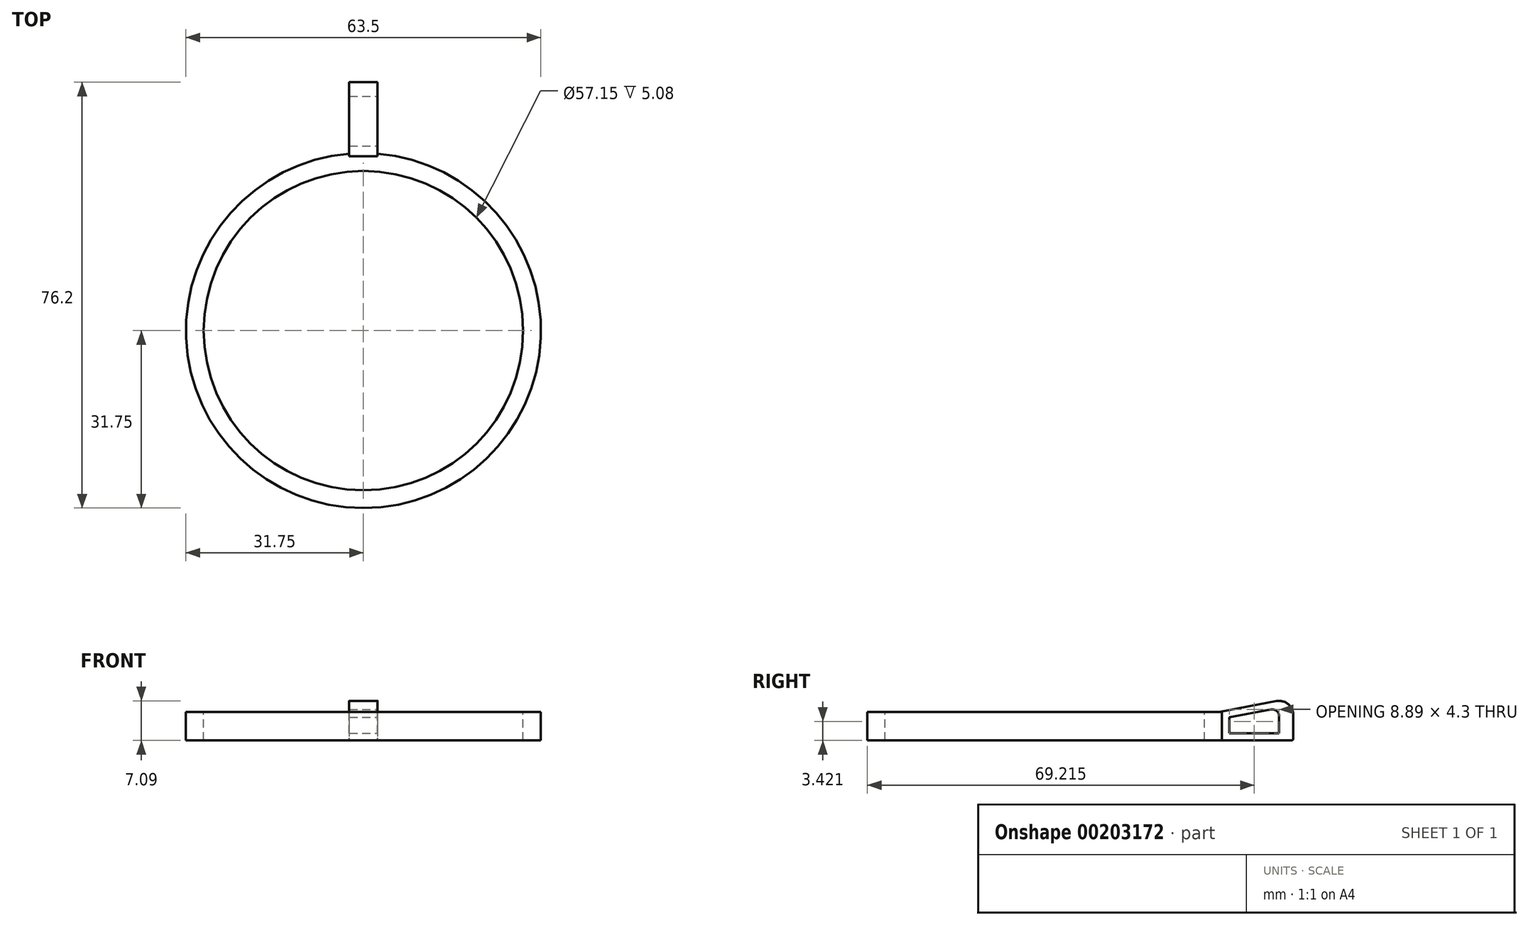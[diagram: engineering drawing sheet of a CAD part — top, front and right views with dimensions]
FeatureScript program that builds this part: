
annotation { "Feature Type Name" : "Feature", "Feature Type Description" : "" }
export const myFeature = defineFeature(function(context is Context, id is Id, definition is map)
    precondition{}
    {
        {
            var Q0;
            Q0=qCreatedBy(makeId("Top.planeOp"),FACE);
            var sketch = newSketch(context, id + "F0", { "sketchPlane" : qUnion([Q0])});
            skCircle(sketch, "E0", {"center": v(0, 0) * mm, "radius": 31.75 * mm});
            skSolve(sketch);
        }
        {
            var Q0;
            Q0=makeQuery(id+"F0.imprint","IMPRINT",FACE,{"disambiguationData":[TD([[makeQuery(id+"F0.imprint","IMPRINT",EDGE,{"derivedFrom":sQuery(id+"F0.wireOp",EDGE,"E0")}),1.0]])]});
            extrude(context, id + "F1", {"entities" : qUnion([Q0]), "depth" : 5.08 * mm});
        }
        {
            var Q0;
            Q0=makeQuery(id+"F1.opExtrude","CAP_FACE",FACE,{"disambiguationData":[OSD([sQuery(id+"F0.wireOp",EDGE,"E0")])],"isStart":false});
            var sketch = newSketch(context, id + "F2", { "sketchPlane" : qUnion([Q0])});
            skCircle(sketch, "E1", {"center": v(0, 0) * mm, "radius": 28.57 * mm});
            skSolve(sketch);
        }
        {
            var Q0;
            Q0=makeQuery(id+"F2.imprint","IMPRINT",FACE,{"disambiguationData":[TD([[makeQuery(id+"F2.imprint","IMPRINT",EDGE,{"derivedFrom":sQuery(id+"F2.wireOp",EDGE,"E1")}),1.0]])]});
            extrude(context, id + "F3", {"entities" : qUnion([Q0]), "operationType" : NewBodyOperationType.REMOVE, "endBound" : BoundingType.UP_TO_NEXT, "oppositeDirection" : true, "depth" : 25.4 * mm});
        }
        {
            var Q0;
            Q0=qCreatedBy(makeId("Right.planeOp"),FACE);
            var sketch = newSketch(context, id + "F4", { "sketchPlane" : qUnion([Q0])});
            skLineSegment(sketch, "E2", {"start": v(29.21, 4.7) * mm, "end": v(41.43, 7.04) * mm});
            skLineSegment(sketch, "E3", {"start": v(44.45, 4.55) * mm, "end": v(44.45, 0) * mm});
            skLineSegment(sketch, "E4", {"start": v(44.45, 0) * mm, "end": v(29.21, 0) * mm});
            skLineSegment(sketch, "E5", {"start": v(29.21, 0) * mm, "end": v(29.21, 4.7) * mm});
            skPoint(sketch, "E6.visualSharp", {"position": v(44.45, 7.62) * mm});
            skArc(sketch, "E6.filletArc", {"start": v(44.45, 4.55) * mm, "mid": v(43.53, 6.5) * mm, "end": v(41.43, 7.04) * mm});
            skSolve(sketch);
        }
        {
            var Q0;
            Q0=makeQuery(id+"F4.imprint","IMPRINT",FACE,{"disambiguationData":[TD([[makeQuery(id+"F4.imprint","IMPRINT",EDGE,{"derivedFrom":sQuery(id+"F4.wireOp",EDGE,"E2")}),-1.0]])]});
            extrude(context, id + "F5", {"entities" : qUnion([Q0]), "operationType" : NewBodyOperationType.ADD, "depth" : 2.54 * mm, "hasSecondDirection" : true, "secondDirectionOppositeDirection" : true, "secondDirectionDepth" : 2.54 * mm});
        }
        {
            var Q0;
            Q0=makeQuery(id+"F5.opExtrude","SWEPT_EDGE",EDGE,{"disambiguationData":[OSD([sQuery(id+"F4.wireOp",EDGE,"E3"),sQuery(id+"F4.wireOp",EDGE,"E4")])]});
            fillet(context, id + "F6", {"entities" : qUnion([Q0]), "radius" : 0.38 * mm, "tangentPropagation" : true, "allowEdgeOverflow" : false});
        }
        {
            var Q0;
            Q0=makeQuery(id+"F5.opExtrude","CAP_FACE",FACE,{"disambiguationData":[OSD([sQuery(id+"F4.wireOp",EDGE,"E2"),sQuery(id+"F4.wireOp",EDGE,"E3"),sQuery(id+"F4.wireOp",EDGE,"E4"),sQuery(id+"F4.wireOp",EDGE,"E5"),sQuery(id+"F4.wireOp",EDGE,"E6.filletArc")])],"isStart":false});
            var sketch = newSketch(context, id + "F7", { "sketchPlane" : qUnion([Q0])});
            skLineSegment(sketch, "E7", {"start": v(33.02, 4.14) * mm, "end": v(40.4, 5.55) * mm});
            skLineSegment(sketch, "E8", {"start": v(41.91, 4.3) * mm, "end": v(41.91, 1.27) * mm});
            skLineSegment(sketch, "E9", {"start": v(41.91, 1.27) * mm, "end": v(33.02, 1.27) * mm});
            skLineSegment(sketch, "E10", {"start": v(33.02, 1.27) * mm, "end": v(33.02, 4.14) * mm});
            skPoint(sketch, "E11.visualSharp", {"position": v(41.91, 5.84) * mm});
            skArc(sketch, "E11.filletArc", {"start": v(41.91, 4.3) * mm, "mid": v(41.45, 5.28) * mm, "end": v(40.4, 5.55) * mm});
            skSolve(sketch);
        }
        {
            var Q0;
            Q0=makeQuery(id+"F7.imprint","IMPRINT",FACE,{"disambiguationData":[TD([[makeQuery(id+"F7.imprint","IMPRINT",EDGE,{"derivedFrom":sQuery(id+"F7.wireOp",EDGE,"E7")}),-1.0]])]});
            extrude(context, id + "F8", {"entities" : qUnion([Q0]), "operationType" : NewBodyOperationType.REMOVE, "oppositeDirection" : true, "depth" : 25.4 * mm});
        }
    });
